# Revit family: QF_RATIONAL_CombiSteamer_iCC_10-11E
name_source: partatom
category: Specialty Equipment
revit_build: Autodesk Revit 2018 (Build: 20170223_1515(x64)
units: mm (PartAtom-declared; Revit-internal decimal feet)

## family parameters
Always vertical = Yes
Cut with Voids When Loaded = No
OmniClass Number = 23.40.40.14.17.11
OmniClass Title = Cookers, Ovens, Stoves
Part Type = Normal
Room Calculation Point = No
Round Connector Dimension = Use Diameter
Shared = No
Work Plane-Based = No

## types (10) — shared parameters
Assembly Code = E1090320
Cold Water Flow = 0.2 L/s
Cold Water Maximum Pressure = 6.0 bar
Cold Water Minimum Pressure = 1.0 bar
Cold Water Size = 1"
Conn Conduit = Yes
Cycle = 50 Hz
Cycle Alternative = 60 Hz
Depth Actual = 30 1/2"
Description = Electrical Combi-steamer (10 x 1/1 GN / 20 x 1/2 GN)
Direct Waste Size = 2"
Height Actual = 40"
Hood Exhaust Hood = Hood : Exhaust Hood
Hood UltraVent = Hood : UltraVent
Hood UltraVent Plus = Hood : UltraVent Plus
Latent Heat Output = 1 kW
Length Actual = 33 1/2"
Manufacturer = RATIONAL AG
Model = iCombi Classic 10-1/1 E
Sensitive Heat Output = 1 kW
Sound Level = 55dBA
Specification by Manufacturer = Hot-air steamer (combi-steamer mode) for most of the cooking methods used in commercial kitchens for the optional use of steam and hot-air, individually, in succession or in combination.
Stand Levelling Kit = Accessories : Levelling Kit
Stand None = Accessories : None
Stand UG I = Accessories : UG I 699
Stand UG I 150 = Accessories : UG I 150
Stand UG I 200 = Accessories : UG I 200
Stand UG II = Accessories : UG II 699
Stand UG III = Accessories : UG III 699
Stand UG III 945 = Accessories : UG III 945
Stand UG IV = Accessories : UG IV 699
URL = www.rational-online.com
Version = 05-2020
Warranty Duration = 2 years
Waste Water Discharge Temperature = 65 °C
Weight = 127.00 kg

## per-type parameters (varying)
| type | FL Amps | Max Overcurrent Protection | Phase | Volts | Watts |
| 10-1/1E 3 AC 220V | 45 A | 50 A | 3 | 220 V | 17300 W |
| 10-1/1E 3NAC 415V | 29 A | 32 A | 3 | 415 V | 20500 W |
| 10-1/1E 3NAC 400V | 27 A | 32 A | 3 | 400 V | 18900 W |
| 10-1/1E 3AC 480V | 23 A | 25 A | 3 | 480 V | 18900 W |
| 10-1/1E 3AC 440V | 25 A | 32 A | 3 | 440 V | 18900 W |
| 10-1/1E 3AC 400V | 27 A | 32 A | 3 | 400 V | 18900 W |
| 10-1/1E 3AC 240V | 49 A | 50 A | 3 | 240 V | 20500 W |
| 10-1/1E 3AC 230V | 47 A | 50 A | 3 | 230 V | 18900 W |
| 10-1/1E 3AC 208V | 53 A | 70 A | 3 | 208 V | 18900 W |
| 10-1/1E 3AC 200V | 48 A | 50 A | 1 | 230 V | 11100 W |

## geometry (parser evidence)
native form markers: Sweep x17
no freeform markers — native parametric forms only
